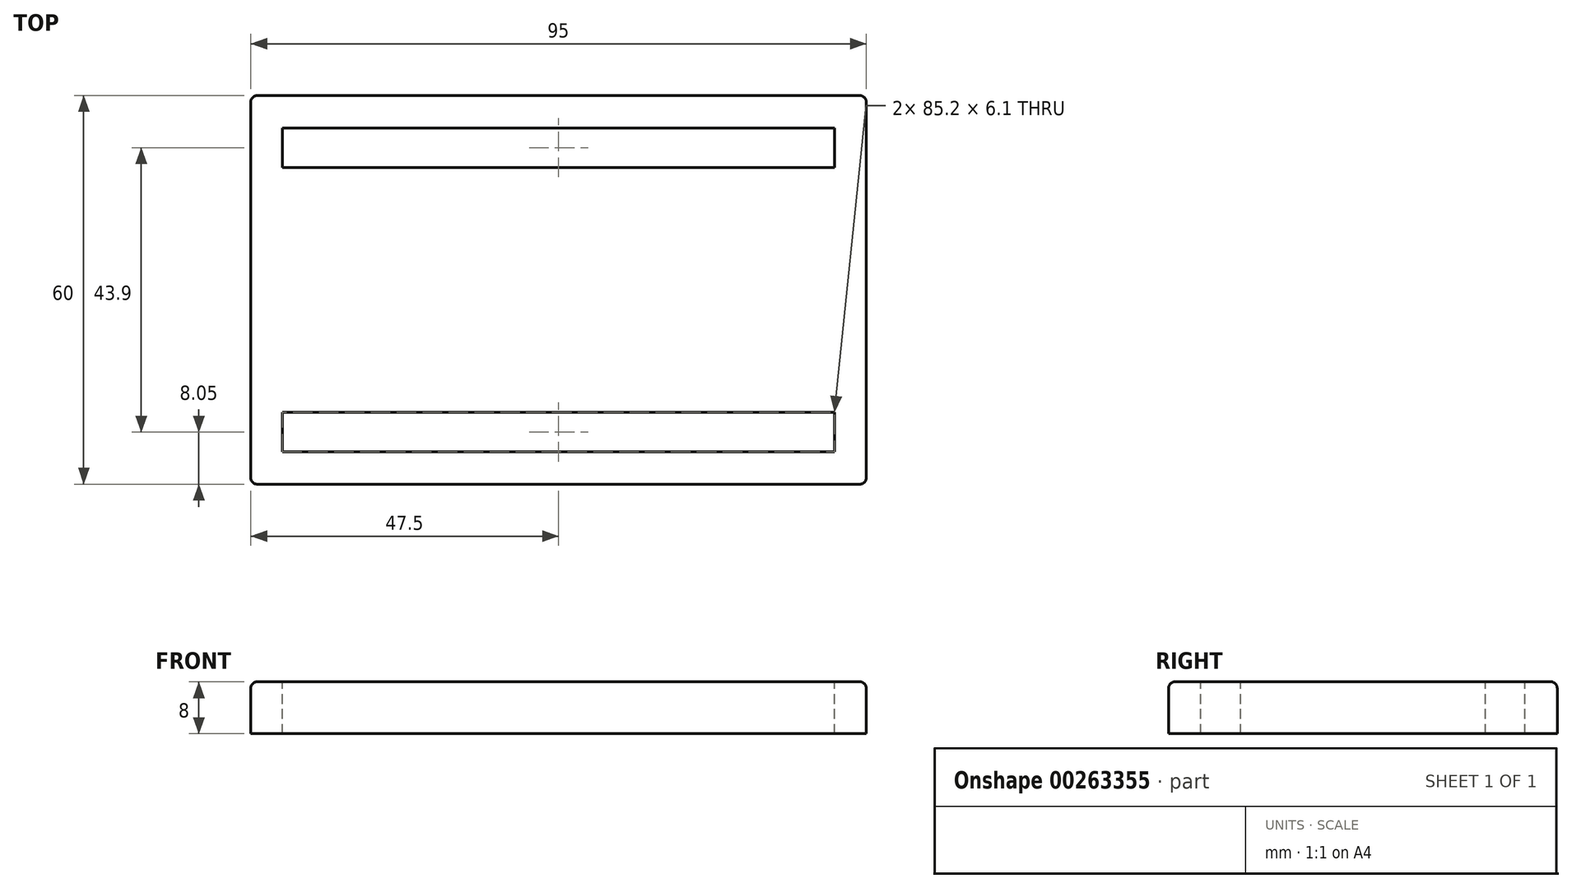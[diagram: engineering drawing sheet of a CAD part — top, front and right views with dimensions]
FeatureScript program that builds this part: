
annotation { "Feature Type Name" : "Feature", "Feature Type Description" : "" }
export const myFeature = defineFeature(function(context is Context, id is Id, definition is map)
    precondition{}
    {
        {
            var Q0;
            Q0=qCreatedBy(makeId("Top.planeOp"),FACE);
            var sketch = newSketch(context, id + "F0", { "sketchPlane" : qUnion([Q0])});
            skLineSegment(sketch, "E0.bottom", {"start": v(0, 0) * mm, "end": v(95, 0) * mm});
            skLineSegment(sketch, "E0.top", {"start": v(0, 60) * mm, "end": v(95, 60) * mm});
            skLineSegment(sketch, "E0.left", {"start": v(0, 0) * mm, "end": v(0, 60) * mm});
            skLineSegment(sketch, "E0.right", {"start": v(95, 0) * mm, "end": v(95, 60) * mm});
            skSolve(sketch);
        }
        {
            var Q0;
            Q0 = qSketchRegion(id + "F0", true);
            extrude(context, id + "F1", {"entities" : qUnion([Q0]), "depth" : 8 * mm});
        }
        {
            var Q0;
            Q0=makeQuery(id+"F1.opExtrude","CAP_FACE",FACE,{"disambiguationData":[OSD([sQuery(id+"F0.wireOp",EDGE,"E0.bottom"),sQuery(id+"F0.wireOp",EDGE,"E0.top"),sQuery(id+"F0.wireOp",EDGE,"E0.left"),sQuery(id+"F0.wireOp",EDGE,"E0.right")])],"isStart":false});
            var sketch = newSketch(context, id + "F2", { "sketchPlane" : qUnion([Q0])});
            skLineSegment(sketch, "E1.bottom", {"start": v(4.9, 55) * mm, "end": v(90.1, 55) * mm});
            skLineSegment(sketch, "E1.top", {"start": v(4.9, 48.9) * mm, "end": v(90.1, 48.9) * mm});
            skLineSegment(sketch, "E1.left", {"start": v(4.9, 55) * mm, "end": v(4.9, 48.9) * mm});
            skLineSegment(sketch, "E1.right", {"start": v(90.1, 55) * mm, "end": v(90.1, 48.9) * mm});
            skLineSegment(sketch, "E2.bottom", {"start": v(4.9, 11.1) * mm, "end": v(90.1, 11.1) * mm});
            skLineSegment(sketch, "E2.top", {"start": v(4.9, 5) * mm, "end": v(90.1, 5) * mm});
            skLineSegment(sketch, "E2.left", {"start": v(4.9, 11.1) * mm, "end": v(4.9, 5) * mm});
            skLineSegment(sketch, "E2.right", {"start": v(90.1, 11.1) * mm, "end": v(90.1, 5) * mm});
            skSolve(sketch);
        }
        {
            var Q0;
            Q0 = qSketchRegion(id + "F2", true);
            extrude(context, id + "F3", {"entities" : qUnion([Q0]), "operationType" : NewBodyOperationType.REMOVE, "oppositeDirection" : true, "depth" : 25 * mm});
        }
        {
            var Q0;
            Q0=makeQuery(id+"F1.opExtrude","SWEPT_EDGE",EDGE,{"disambiguationData":[OSD([sQuery(id+"F0.wireOp",EDGE,"E0.top"),sQuery(id+"F0.wireOp",EDGE,"E0.left")])]});
            var Q1;
            Q1=makeQuery(id+"F1.opExtrude","SWEPT_EDGE",EDGE,{"disambiguationData":[OSD([sQuery(id+"F0.wireOp",EDGE,"E0.bottom"),sQuery(id+"F0.wireOp",EDGE,"E0.left")])]});
            var Q2;
            Q2=makeQuery(id+"F1.opExtrude","SWEPT_EDGE",EDGE,{"disambiguationData":[OSD([sQuery(id+"F0.wireOp",EDGE,"E0.bottom"),sQuery(id+"F0.wireOp",EDGE,"E0.right")])]});
            var Q3;
            Q3=makeQuery(id+"F1.opExtrude","SWEPT_EDGE",EDGE,{"disambiguationData":[OSD([sQuery(id+"F0.wireOp",EDGE,"E0.top"),sQuery(id+"F0.wireOp",EDGE,"E0.right")])]});
            var Q4;
            Q4=makeQuery(id+"F1.opExtrude","CAP_EDGE",EDGE,{"disambiguationData":[OSD([sQuery(id+"F0.wireOp",EDGE,"E0.left")])],"isStart":false});
            var Q5;
            Q5=makeQuery(id+"F1.opExtrude","CAP_EDGE",EDGE,{"disambiguationData":[OSD([sQuery(id+"F0.wireOp",EDGE,"E0.bottom")])],"isStart":false});
            var Q6;
            Q6=makeQuery(id+"F1.opExtrude","CAP_EDGE",EDGE,{"disambiguationData":[OSD([sQuery(id+"F0.wireOp",EDGE,"E0.right")])],"isStart":false});
            var Q7;
            Q7=makeQuery(id+"F1.opExtrude","CAP_EDGE",EDGE,{"disambiguationData":[OSD([sQuery(id+"F0.wireOp",EDGE,"E0.top")])],"isStart":false});
            fillet(context, id + "F4", {"entities" : qUnion([Q0, Q1, Q2, Q3, Q4, Q5, Q6, Q7]), "radius" : 1 * mm, "tangentPropagation" : true, "allowEdgeOverflow" : false});
        }
    });
